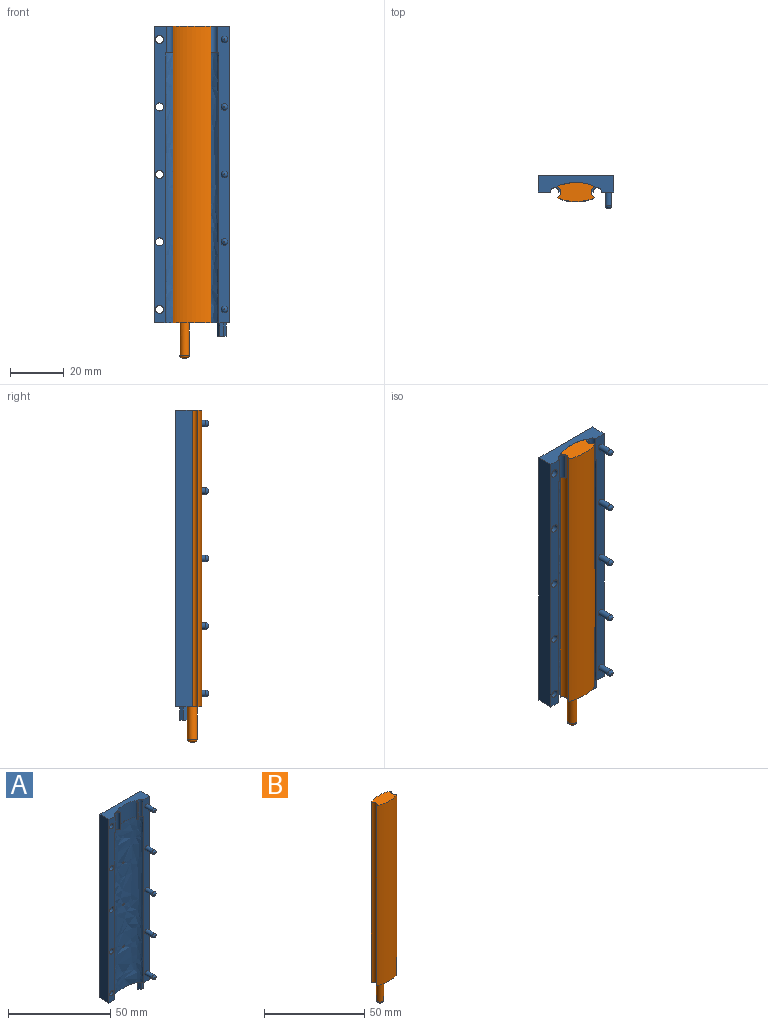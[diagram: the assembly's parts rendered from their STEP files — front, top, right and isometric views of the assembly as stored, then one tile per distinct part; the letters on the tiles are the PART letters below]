
ASSEMBLY  parts=2 mates=1
PART A: 55 faces, bbox 28x12.2x115 mm
  f0: plane 9.5x4mm, normal (0,0,-1), area 7.7mm2, adj f2,f7,f12,f13,f14,f15,f51
  f1: plane 28x6.2mm, normal (0,0,-1), area 96.3mm2, adj f2,f3,f4,f5,f6,f7,f17,f18
  f2: plane 110x4.5mm, normal (0,-1,0), area 422.4mm2, adj f0,f1,f3,f7,f15,f16,f36,f38
  f3: plane 110x6.2mm, normal (1,0,0), area 682.5mm2, adj f1,f2,f4,f16
  f4: plane 110x28mm, normal (0,1,0), area 3041.5mm2, adj f1,f3,f5,f16,f31,f32,f33,f34
  f5: plane 110x6.2mm, normal (-1,0,0), area 682.5mm2, adj f1,f4,f6,f16
  f6: plane 110x4.5mm, normal (0,-1,0), area 409.7mm2, adj f1,f5,f7,f8,f9,f16,f31,f32
  f7: extruded ~100x20mm, area 2298.6mm2, adj f0,f1,f2,f6,f8,f51,f52,f53
  f8: plane 9.5x4mm, normal (0,0,-1), area 7.7mm2, adj f6,f7,f9,f10,f11,f12,f51
  f9: cylinder r=1.6mm len=10mm, axis (0,0,-1), area 50.3mm2, adj f6,f8,f10,f16
  f10: plane 10x0.6mm, normal (0,-1,0), area 6mm2, adj f8,f9,f11,f16
  f11: cylinder r=2.2mm len=10mm, axis (0,0,-1), area 25.1mm2, adj f8,f10,f12,f16
  f12: extruded ~13.96x10mm, area 143.9mm2, adj f0,f8,f11,f13,f16,f51
  f13: cylinder r=2.2mm len=10mm, axis (0,0,-1), area 25.1mm2, adj f0,f12,f14,f16
  f14: plane 10x0.6mm, normal (0,-1,0), area 6mm2, adj f0,f13,f15,f16
  f15: cylinder r=1.6mm len=10mm, axis (0,0,-1), area 50.3mm2, adj f0,f2,f14,f16
  f16: plane 28x6.2mm, normal (0,0,1), area 126.8mm2, adj f2,f3,f4,f5,f6,f9,f10,f11
  f17: plane 6x1.5mm, normal (-0.87,0.5,0), area 10.4mm2, adj f1,f18,f22,f23
  f18: plane 6x1.73mm, normal (0,1,0), area 7.6mm2, adj f1,f17,f19,f23,f31
  f19: plane 3.69x1.5mm, normal (0.87,0.5,0), area 6.2mm2, adj f1,f18,f20,f31
  f20: plane 3.69x1.5mm, normal (0.87,-0.5,0), area 6.2mm2, adj f1,f19,f21,f31
  f21: plane 6x1.73mm, normal (0,-1,0), area 7.6mm2, adj f1,f20,f22,f23,f31
  f22: plane 6x1.5mm, normal (-0.87,-0.5,0), area 10.4mm2, adj f1,f17,f21,f23
  f23: plane 3x1.61mm, normal (0,0,-1), area 3.5mm2, adj f17,f18,f21,f22,f31
  f24: plane 5x1.4mm, normal (0.87,-0.5,0), area 8.1mm2, adj f1,f25,f29,f30
  f25: plane 5x1.62mm, normal (0,-1,0), area 8.1mm2, adj f1,f24,f26,f30
  f26: plane 5x1.4mm, normal (-0.87,-0.5,0), area 8.1mm2, adj f1,f25,f27,f30
  f27: plane 5x1.4mm, normal (-0.87,0.5,0), area 8.1mm2, adj f1,f26,f28,f30
  f28: plane 5x1.62mm, normal (0,1,0), area 8.1mm2, adj f1,f27,f29,f30
  f29: plane 5x1.4mm, normal (0.87,0.5,0), area 8.1mm2, adj f1,f24,f28,f30
  f30: plane 3.23x2.8mm, normal (0,0,-1), area 6.8mm2, adj f24,f25,f26,f27,f28,f29
  f31: cylinder r=1.5mm len=6.2mm, axis (0,-1,0), area 47.2mm2, adj f4,f6,f18,f19,f20,f21,f23
  f32: cylinder r=1.5mm len=6.2mm, axis (0,-1,0), area 58.5mm2, adj f4,f6
  f33: cylinder r=1.5mm len=6.2mm, axis (0,-1,0), area 58.5mm2, adj f4,f6
  f34: cylinder r=1.5mm len=6.2mm, axis (0,-1,0), area 58.5mm2, adj f4,f6
  f35: cylinder r=1.5mm len=6.2mm, axis (0,-1,0), area 58.5mm2, adj f4,f6
  f36: cylinder r=1.2mm len=5mm, axis (0,1,0), area 37.7mm2, adj f2,f49
  f37: plane 0.4x0.4mm, normal (0,-1,0), area 0.1mm2, adj f49
  f38: cylinder r=1.2mm len=5mm, axis (0,1,0), area 37.7mm2, adj f2,f48
  f39: plane 0.4x0.4mm, normal (0,-1,0), area 0.1mm2, adj f48
  f40: cylinder r=1.2mm len=5mm, axis (0,1,0), area 37.7mm2, adj f2,f47
  f41: plane 0.4x0.4mm, normal (0,-1,0), area 0.1mm2, adj f47
  f42: cylinder r=1.2mm len=5mm, axis (0,1,0), area 37.7mm2, adj f2,f50
  f43: plane 0.4x0.4mm, normal (0,-1,0), area 0.1mm2, adj f50
  f44: cylinder r=1.2mm len=5mm, axis (0,1,0), area 37.7mm2, adj f2,f46
  f45: plane 0.4x0.4mm, normal (0,-1,0), area 0.1mm2, adj f46
  f46: torus R=0.2mm, axis (0,-1,0), area 8.3mm2, adj f44,f45
  f47: torus R=0.2mm, axis (0,-1,0), area 8.3mm2, adj f40,f41
  f48: torus R=0.2mm, axis (0,-1,0), area 8.3mm2, adj f38,f39
  f49: torus R=0.2mm, axis (0,-1,0), area 8.3mm2, adj f36,f37
  f50: torus R=0.2mm, axis (0,-1,0), area 8.3mm2, adj f42,f43
  f51: cylinder r=0.5mm len=2.71mm, axis (0,1,0), area 7.7mm2, adj f0,f4,f7,f8,f12
  f52: cylinder r=0.5mm len=2.2mm, axis (0,1,0), area 6.9mm2, adj f4,f7
  f53: cylinder r=0.5mm len=2.2mm, axis (0,1,0), area 6.9mm2, adj f4,f7
  f54: cylinder r=0.5mm len=2.2mm, axis (0,1,0), area 6.9mm2, adj f4,f7
PART B: 11 faces, bbox 14x7x123 mm
  f0: cylinder r=2.2mm len=110mm, axis (0,0,-1), area 551.2mm2, adj f1,f3,f4,f5
  f1: extruded ~110x13.96mm, area 1587.1mm2, adj f0,f2,f4,f5
  f2: cylinder r=2.2mm len=110mm, axis (0,0,-1), area 551.2mm2, adj f1,f3,f4,f5
  f3: extruded ~110x13.96mm, area 1587.1mm2, adj f0,f2,f4,f5
  f4: plane 13.96x7mm, normal (0,0,1), area 77.9mm2, adj f0,f1,f2,f3
  f5: plane 13.96x7mm, normal (0,0,-1), area 55.1mm2, adj f0,f1,f2,f3,f6,f8
  f6: cylinder r=2mm len=15mm, axis (0,0,-1), area 188.5mm2, adj f5,f7
  f7: plane 4x4mm, normal (0,0,-1), area 12.6mm2, adj f6
  f8: cylinder r=1.8mm len=12mm, axis (0,0,1), area 135.7mm2, adj f5,f10
  f9: plane 1.6x1.6mm, normal (0,0,-1), area 2mm2, adj f10
  f10: torus R=0.8mm, axis (0,0,-1), area 14.2mm2, adj f8,f9
PLACE A t=(-65.29,-3.65,-1.28)mm fixed
PLACE B t=(-65.29,-3.65,-1.28)mm
MATE planar B.f4 <-> A.f16  axis (0,0,1) through (-65.29,-3.65,108.72)mm
